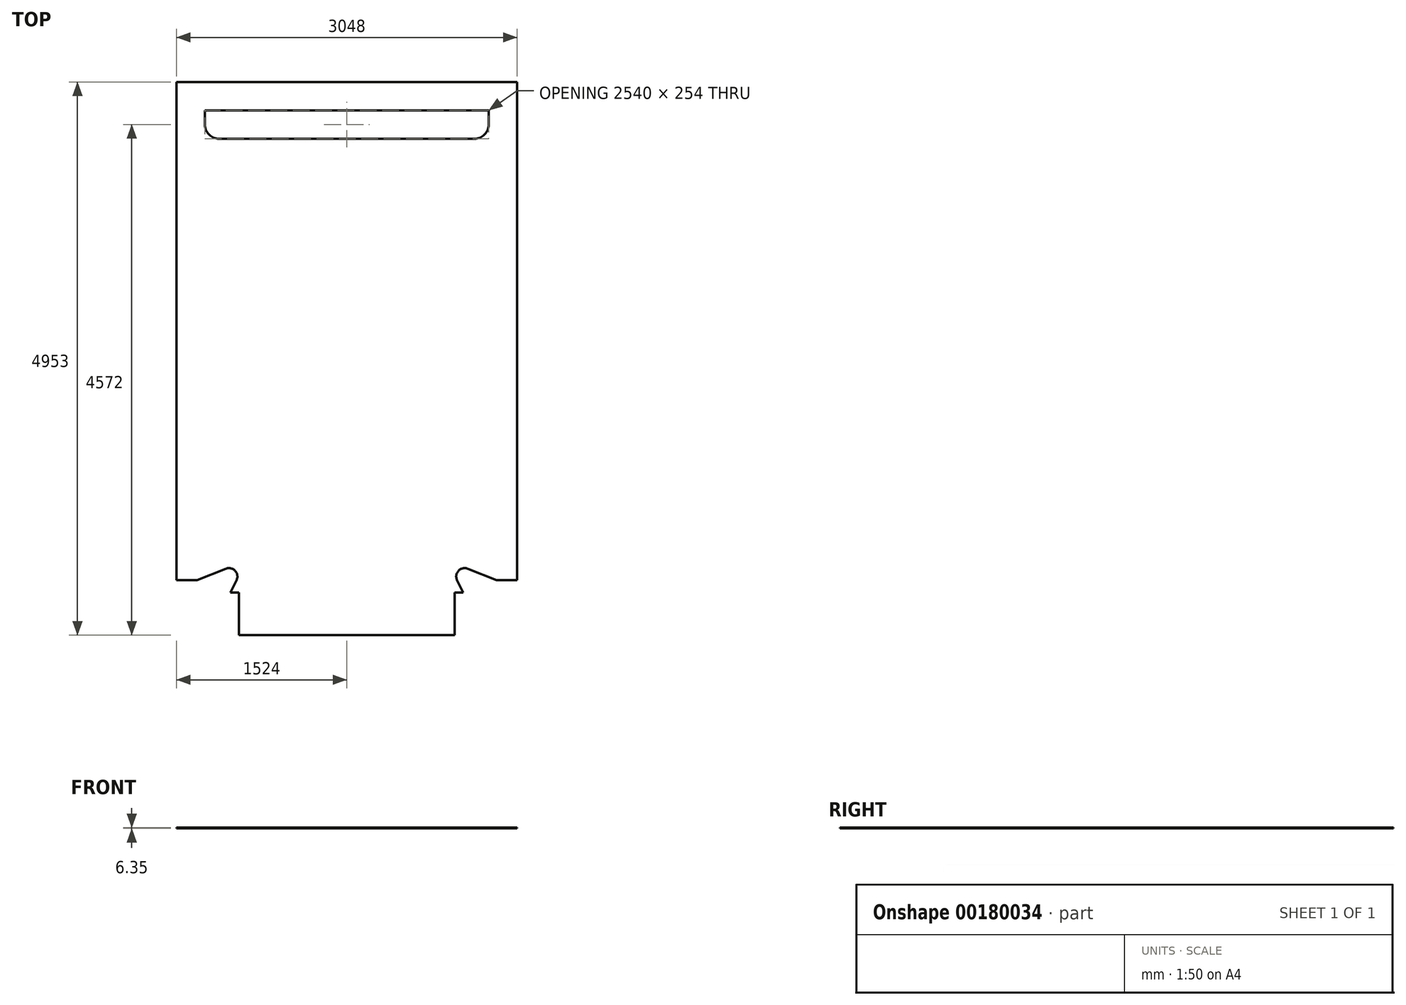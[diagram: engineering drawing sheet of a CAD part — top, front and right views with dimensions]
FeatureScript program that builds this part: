
annotation { "Feature Type Name" : "Feature", "Feature Type Description" : "" }
export const myFeature = defineFeature(function(context is Context, id is Id, definition is map)
    precondition{}
    {
        {
            var Q0;
            Q0=qCreatedBy(makeId("Top.planeOp"),FACE);
            var sketch = newSketch(context, id + "F0", { "sketchPlane" : qUnion([Q0])});
            skArc(sketch, "E0", {"start": v(349.92, 1812.83) * mm, "mid": v(439.73, 1850.03) * mm, "end": v(476.92, 1939.83) * mm});
            skArc(sketch, "E1", {"start": v(476.92, 1939.83) * mm, "mid": v(439.73, 2029.63) * mm, "end": v(349.92, 2066.83) * mm});
            skLineSegment(sketch, "E2", {"start": v(349.92, 2066.83) * mm, "end": v(-1936.08, 2066.83) * mm});
            skArc(sketch, "E3", {"start": v(-1936.08, 2066.83) * mm, "mid": v(-2025.88, 2029.63) * mm, "end": v(-2063.08, 1939.83) * mm});
            skArc(sketch, "E4", {"start": v(-2063.08, 1939.83) * mm, "mid": v(-2025.88, 1850.03) * mm, "end": v(-1936.08, 1812.83) * mm});
            skLineSegment(sketch, "E5", {"start": v(-1936.08, 1812.83) * mm, "end": v(349.92, 1812.83) * mm});
            skLineSegment(sketch, "E6", {"start": v(248.32, -2251.17) * mm, "end": v(194.06, -2141.82) * mm});
            skArc(sketch, "E7", {"start": v(194.06, -2141.82) * mm, "mid": v(206.29, -2056.3) * mm, "end": v(290.53, -2037.16) * mm});
            skLineSegment(sketch, "E8", {"start": v(290.53, -2037.16) * mm, "end": v(546.45, -2139.16) * mm});
            skLineSegment(sketch, "E9", {"start": v(546.45, -2139.16) * mm, "end": v(730.92, -2139.16) * mm});
            skLineSegment(sketch, "E10", {"start": v(730.92, -2139.16) * mm, "end": v(730.92, 2320.83) * mm});
            skLineSegment(sketch, "E11", {"start": v(730.92, 2320.83) * mm, "end": v(-2317.08, 2320.83) * mm});
            skLineSegment(sketch, "E12", {"start": v(-2317.08, 2320.83) * mm, "end": v(-2317.08, -2139.16) * mm});
            skLineSegment(sketch, "E13", {"start": v(-2317.08, -2139.16) * mm, "end": v(-2132.6, -2139.16) * mm});
            skLineSegment(sketch, "E14", {"start": v(-2132.6, -2139.16) * mm, "end": v(-1876.68, -2037.16) * mm});
            skArc(sketch, "E15", {"start": v(-1876.68, -2037.16) * mm, "mid": v(-1792.44, -2056.3) * mm, "end": v(-1780.21, -2141.82) * mm});
            skLineSegment(sketch, "E16", {"start": v(-1780.21, -2141.82) * mm, "end": v(-1834.48, -2251.17) * mm});
            skLineSegment(sketch, "E17", {"start": v(-1834.48, -2251.17) * mm, "end": v(-1758.28, -2251.17) * mm});
            skLineSegment(sketch, "E18", {"start": v(-1758.28, -2251.17) * mm, "end": v(-1758.28, -2632.17) * mm});
            skLineSegment(sketch, "E19", {"start": v(-1758.28, -2632.17) * mm, "end": v(172.12, -2632.17) * mm});
            skLineSegment(sketch, "E20", {"start": v(172.12, -2632.17) * mm, "end": v(172.12, -2251.17) * mm});
            skLineSegment(sketch, "E21", {"start": v(172.12, -2251.17) * mm, "end": v(248.32, -2251.17) * mm});
            skArc(sketch, "E22", {"start": v(-69.78, -2098.77) * mm, "mid": v(78.5, -1831.5) * mm, "end": v(382.57, -1800.41) * mm});
            skLineSegment(sketch, "E23", {"start": v(382.57, -1800.41) * mm, "end": v(476.92, -1838.02) * mm});
            skLineSegment(sketch, "E24", {"start": v(476.92, -1838.02) * mm, "end": v(476.92, 2066.83) * mm});
            skLineSegment(sketch, "E25", {"start": v(476.92, 2066.83) * mm, "end": v(-2063.08, 2066.83) * mm});
            skLineSegment(sketch, "E26", {"start": v(-2063.08, 2066.83) * mm, "end": v(-2063.08, -1838.02) * mm});
            skLineSegment(sketch, "E27", {"start": v(-2063.08, -1838.02) * mm, "end": v(-1968.72, -1800.41) * mm});
            skArc(sketch, "E28", {"start": v(-1968.72, -1800.41) * mm, "mid": v(-1664.66, -1831.5) * mm, "end": v(-1516.38, -2098.77) * mm});
            skLineSegment(sketch, "E29", {"start": v(-1516.38, -2098.77) * mm, "end": v(-1504.28, -2098.77) * mm});
            skLineSegment(sketch, "E30", {"start": v(-1504.28, -2098.77) * mm, "end": v(-1504.28, -2632.17) * mm});
            skLineSegment(sketch, "E31", {"start": v(-1504.28, -2632.17) * mm, "end": v(-81.88, -2632.17) * mm});
            skLineSegment(sketch, "E32", {"start": v(-81.88, -2632.17) * mm, "end": v(-81.88, -2098.77) * mm});
            skLineSegment(sketch, "E33", {"start": v(-81.88, -2098.77) * mm, "end": v(-69.78, -2098.77) * mm});
            skSolve(sketch);
        }
        {
            var Q0;
            Q0 = qSketchRegion(id + "F0", true);
            extrude(context, id + "F1", {"entities" : qUnion([Q0]), "depth" : 6.35 * mm});
        }
    });
